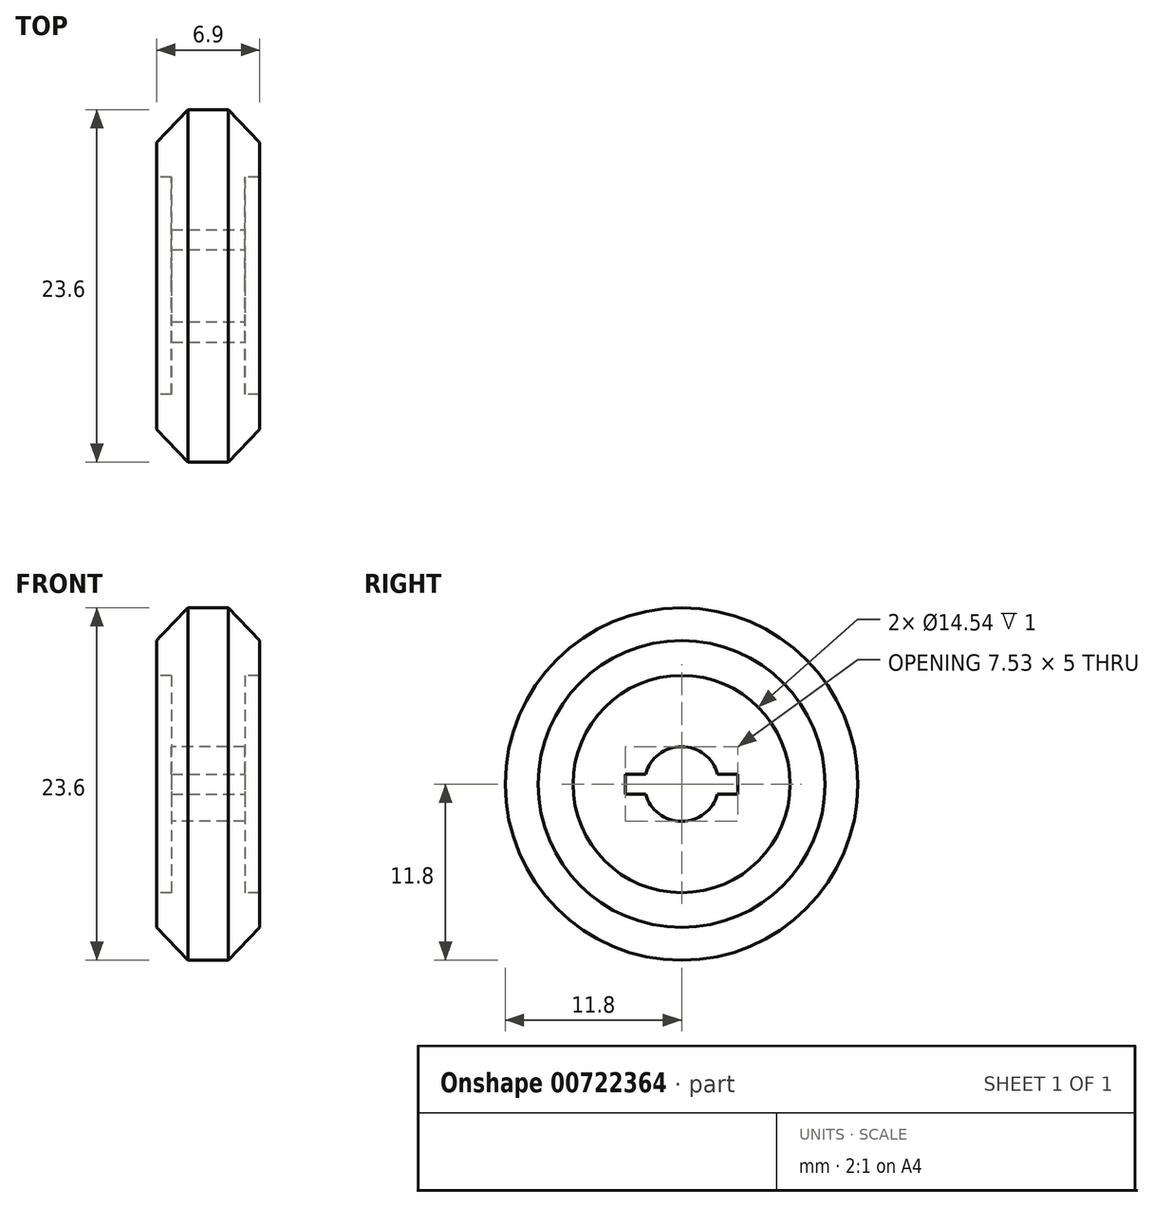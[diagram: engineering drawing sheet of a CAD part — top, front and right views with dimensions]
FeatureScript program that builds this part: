
annotation { "Feature Type Name" : "Feature", "Feature Type Description" : "" }
export const myFeature = defineFeature(function(context is Context, id is Id, definition is map)
    precondition{}
    {
        {
            var Q0;
            Q0=qCreatedBy(makeId("Front.planeOp"),FACE);
            var sketch = newSketch(context, id + "F0", { "sketchPlane" : qUnion([Q0])});
            skLineSegment(sketch, "E0", {"start": v(0, 0) * mm, "end": v(0, 11.8) * mm, "construction": true});
            skLineSegment(sketch, "E1", {"start": v(0, 11.8) * mm, "end": v(1.35, 11.8) * mm});
            skLineSegment(sketch, "E2", {"start": v(1.35, 11.8) * mm, "end": v(3.45, 9.6) * mm});
            skLineSegment(sketch, "E3", {"start": v(3.45, 9.6) * mm, "end": v(3.45, 7.27) * mm});
            skLineSegment(sketch, "E4", {"start": v(2.45, 2.5) * mm, "end": v(-2.45, 2.5) * mm});
            skLineSegment(sketch, "E5.MirrorCS", {"start": v(-3.45, 9.6) * mm, "end": v(-3.45, 7.27) * mm});
            skLineSegment(sketch, "E6.MirrorCS", {"start": v(-1.35, 11.8) * mm, "end": v(-3.45, 9.6) * mm});
            skLineSegment(sketch, "E7.MirrorCS", {"start": v(0, 11.8) * mm, "end": v(-1.35, 11.8) * mm});
            skLineSegment(sketch, "E8", {"start": v(-8.66, 0) * mm, "end": v(9.08, 0) * mm});
            skLineSegment(sketch, "E9", {"start": v(-3.45, 7.27) * mm, "end": v(-2.45, 7.27) * mm});
            skLineSegment(sketch, "E10", {"start": v(-2.45, 7.27) * mm, "end": v(-2.45, 2.5) * mm});
            skLineSegment(sketch, "E11.MirrorCS", {"start": v(2.45, 7.27) * mm, "end": v(2.45, 2.5) * mm});
            skLineSegment(sketch, "E12.MirrorCS", {"start": v(3.45, 7.27) * mm, "end": v(2.45, 7.27) * mm});
            skPoint(sketch, "E13.orphan", {"position": v(-3.45, 2.5) * mm});
            skPoint(sketch, "E14.orphan", {"position": v(3.45, 2.5) * mm});
            skSolve(sketch);
        }
        {
            var Q0;
            Q0=makeQuery(id+"F0.imprint","IMPRINT",FACE,{"disambiguationData":[TD([[makeQuery(id+"F0.imprint","IMPRINT",EDGE,{"derivedFrom":sQuery(id+"F0.wireOp",EDGE,"E1")}),-1.0]])]});
            var Q1;
            Q1=sQuery(id+"F0.wireOp",EDGE,"E8");
            revolve(context, id + "F1", {"entities" : qUnion([Q0]), "axis" : qUnion([Q1]), "revolveType" : RevolveType.FULL});
        }
        {
            var Q0;
            Q0=makeQuery(id+"F1.opRevolve","SWEPT_FACE",FACE,{"disambiguationData":[OSD([sQuery(id+"F0.wireOp",EDGE,"E11.MirrorCS")])]});
            var sketch = newSketch(context, id + "F2", { "sketchPlane" : qUnion([Q0])});
            skLineSegment(sketch, "E15.bottom", {"start": v(-3.76, 0.67) * mm, "end": v(3.76, 0.67) * mm});
            skLineSegment(sketch, "E15.top", {"start": v(-3.76, -0.67) * mm, "end": v(3.76, -0.67) * mm});
            skLineSegment(sketch, "E15.left", {"start": v(-3.76, 0.67) * mm, "end": v(-3.76, -0.67) * mm});
            skLineSegment(sketch, "E15.right", {"start": v(3.76, 0.67) * mm, "end": v(3.76, -0.67) * mm});
            skLineSegment(sketch, "E16", {"start": v(-3.76, 0.67) * mm, "end": v(3.76, -0.67) * mm, "construction": true});
            skSolve(sketch);
        }
        {
            var Q0;
            {var subQ0=sQuery(id+"F2.wireOp",EDGE,"E15.left");Q0=makeQuery(id+"F2.imprint","IMPRINT",FACE,{"disambiguationData":[TD([[makeQuery(id+"F2.imprint","IMPRINT",EDGE,{"derivedFrom":subQ0}),1.0]])]});}
            var Q1;
            {var subQ0=sQuery(id+"F2.wireOp",EDGE,"E15.right");Q1=makeQuery(id+"F2.imprint","IMPRINT",FACE,{"disambiguationData":[TD([[makeQuery(id+"F2.imprint","IMPRINT",EDGE,{"derivedFrom":subQ0}),-1.0]])]});}
            extrude(context, id + "F3", {"entities" : qUnion([Q0, Q1]), "operationType" : NewBodyOperationType.REMOVE, "endBound" : BoundingType.THROUGH_ALL, "oppositeDirection" : true, "depth" : 25 * mm, "offsetDistance" : 25 * mm});
        }
    });
